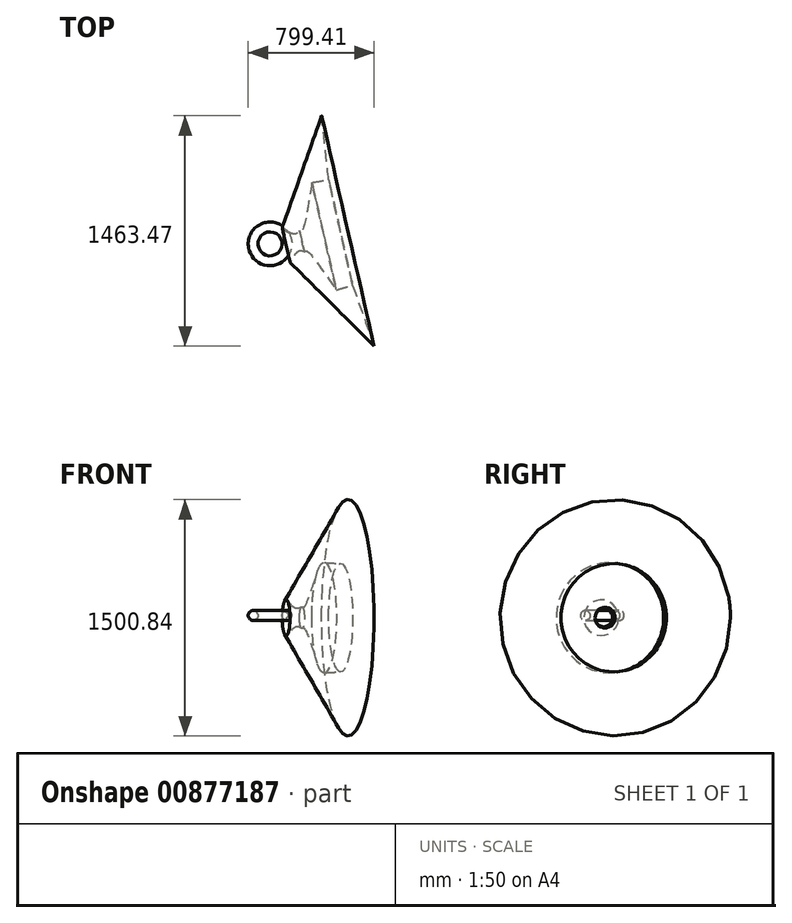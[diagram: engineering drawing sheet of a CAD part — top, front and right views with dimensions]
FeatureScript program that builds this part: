
annotation { "Feature Type Name" : "Feature", "Feature Type Description" : "" }
export const myFeature = defineFeature(function(context is Context, id is Id, definition is map)
    precondition{}
    {
        {
            var Q0;
            Q0=qCreatedBy(makeId("Top.planeOp"),FACE);
            var sketch = newSketch(context, id + "F0", { "sketchPlane" : qUnion([Q0])});
            skCircle(sketch, "E0", {"center": v(25.63, 92.78) * mm, "radius": 23.44 * mm});
            skCircle(sketch, "E1.cCircle", {"center": v(-37.7, 45.85) * mm, "radius": 25.25 * mm, "construction": true});
            skLineSegment(sketch, "E1.0", {"start": v(-35.04, 19.98) * mm, "end": v(-47.37, 21.7) * mm});
            skLineSegment(sketch, "E1.1", {"start": v(-47.37, 21.7) * mm, "end": v(-57.48, 28.96) * mm});
            skLineSegment(sketch, "E1.2", {"start": v(-57.48, 28.96) * mm, "end": v(-63.06, 40.08) * mm});
            skLineSegment(sketch, "E1.3", {"start": v(-63.06, 40.08) * mm, "end": v(-62.84, 52.52) * mm});
            skLineSegment(sketch, "E1.4", {"start": v(-62.84, 52.52) * mm, "end": v(-56.86, 63.44) * mm});
            skLineSegment(sketch, "E1.5", {"start": v(-56.86, 63.44) * mm, "end": v(-46.49, 70.32) * mm});
            skLineSegment(sketch, "E1.6", {"start": v(-46.49, 70.32) * mm, "end": v(-34.1, 71.6) * mm});
            skLineSegment(sketch, "E1.7", {"start": v(-34.1, 71.6) * mm, "end": v(-22.55, 66.97) * mm});
            skLineSegment(sketch, "E1.8", {"start": v(-22.55, 66.97) * mm, "end": v(-14.47, 57.51) * mm});
            skLineSegment(sketch, "E1.9", {"start": v(-14.47, 57.51) * mm, "end": v(-11.71, 45.38) * mm});
            skLineSegment(sketch, "E1.10", {"start": v(-11.71, 45.38) * mm, "end": v(-14.9, 33.35) * mm});
            skLineSegment(sketch, "E1.11", {"start": v(-14.9, 33.35) * mm, "end": v(-23.33, 24.18) * mm});
            skLineSegment(sketch, "E1.12", {"start": v(-23.33, 24.18) * mm, "end": v(-35.04, 19.98) * mm});
            skPoint(sketch, "E1.0.midPoint", {"position": v(-41.2, 20.84) * mm});
            skCircle(sketch, "E2.cCircle", {"center": v(-11.71, 45.38) * mm, "radius": 29.2 * mm, "construction": true});
            skLineSegment(sketch, "E2.0", {"start": v(14.08, 63.64) * mm, "end": v(19.44, 40.06) * mm});
            skLineSegment(sketch, "E2.1", {"start": v(19.44, 40.06) * mm, "end": v(6.56, 19.59) * mm});
            skLineSegment(sketch, "E2.2", {"start": v(6.56, 19.59) * mm, "end": v(-17.03, 14.22) * mm});
            skLineSegment(sketch, "E2.3", {"start": v(-17.03, 14.22) * mm, "end": v(-37.5, 27.1) * mm});
            skLineSegment(sketch, "E2.4", {"start": v(-37.5, 27.1) * mm, "end": v(-42.86, 50.7) * mm});
            skLineSegment(sketch, "E2.5", {"start": v(-42.86, 50.7) * mm, "end": v(-29.98, 71.17) * mm});
            skLineSegment(sketch, "E2.6", {"start": v(-29.98, 71.17) * mm, "end": v(-6.4, 76.53) * mm});
            skLineSegment(sketch, "E2.7", {"start": v(-6.4, 76.53) * mm, "end": v(14.08, 63.64) * mm});
            skPoint(sketch, "E2.0.midPoint", {"position": v(16.76, 51.85) * mm});
            skSolve(sketch);
        }
        {
            var Q0;
            Q0=qCreatedBy(makeId("Right.planeOp"),FACE);
            var sketch = newSketch(context, id + "F1", { "sketchPlane" : qUnion([Q0])});
            skCircle(sketch, "E3", {"center": v(-61.48, 14.32) * mm, "radius": 31.27 * mm});
            skSolve(sketch);
        }
        {
            var Q0;
            Q0=makeQuery(id+"F1.imprint","IMPRINT",FACE,{"disambiguationData":[TD([[makeQuery(id+"F1.imprint","IMPRINT",EDGE,{"derivedFrom":sQuery(id+"F1.wireOp",EDGE,"E3")}),1.0]])]});
            var Q1;
            Q1=sQuery(id+"F0.wireOp",EDGE,"E2.cCircle");
            revolve(context, id + "F2", {"surfaceOperationType" : NewSurfaceOperationType.NEW, "entities" : qUnion([Q0]), "axis" : qUnion([Q1]), "revolveType" : RevolveType.FULL});
        }
        {
            var Q0;
            Q0=qCreatedBy(makeId("Front.planeOp"),FACE);
            var sketch = newSketch(context, id + "F3", { "sketchPlane" : qUnion([Q0])});
            skLineSegment(sketch, "E4", {"start": v(204.9, -28.2) * mm, "end": v(353.17, 336.87) * mm});
            skLineSegment(sketch, "E5", {"start": v(204.9, -28.2) * mm, "end": v(98.97, 106.64) * mm});
            skLineSegment(sketch, "E6", {"start": v(98.97, 106.64) * mm, "end": v(511.75, 738.87) * mm});
            skLineSegment(sketch, "E7", {"start": v(511.75, 738.87) * mm, "end": v(463.23, 322.06) * mm});
            skLineSegment(sketch, "E8", {"start": v(463.23, 322.06) * mm, "end": v(353.17, 336.87) * mm});
            skSolve(sketch);
        }
        {
            var Q0;
            Q0 = qSketchRegion(id + "F3", true);
            var Q1;
            Q1=sQuery(id+"F0.wireOp",EDGE,"E2.2");
            revolve(context, id + "F4", {"operationType" : NewBodyOperationType.ADD, "surfaceOperationType" : NewSurfaceOperationType.NEW, "entities" : qUnion([Q0]), "axis" : qUnion([Q1]), "revolveType" : RevolveType.FULL});
        }
    });
